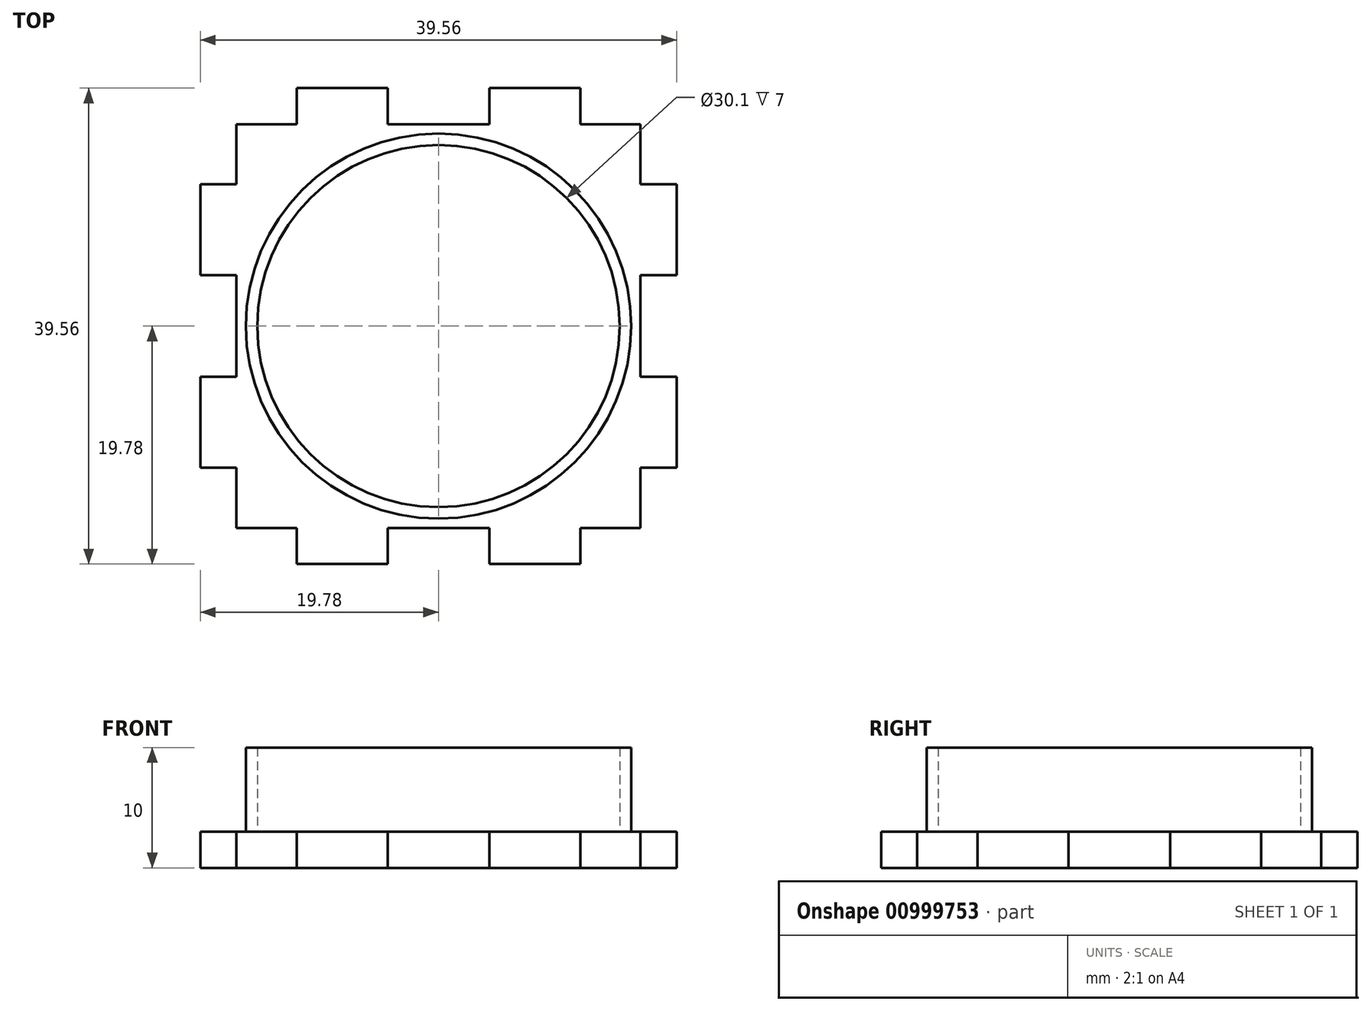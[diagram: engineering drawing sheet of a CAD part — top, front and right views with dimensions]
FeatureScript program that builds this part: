
annotation { "Feature Type Name" : "Feature", "Feature Type Description" : "" }
export const myFeature = defineFeature(function(context is Context, id is Id, definition is map)
    precondition{}
    {
        {
            var Q0;
            Q0=qCreatedBy(makeId("Top.planeOp"),FACE);
            var sketch = newSketch(context, id + "F0", { "sketchPlane" : qUnion([Q0])});
            skLineSegment(sketch, "E0.bottom", {"start": v(17, -17) * mm, "end": v(-17, -17) * mm});
            skLineSegment(sketch, "E0.top", {"start": v(17, 17) * mm, "end": v(-17, 17) * mm});
            skLineSegment(sketch, "E0.left", {"start": v(17, -17) * mm, "end": v(17, 17) * mm});
            skLineSegment(sketch, "E0.right", {"start": v(-17, -17) * mm, "end": v(-17, 17) * mm});
            skPoint(sketch, "E0.middle", {"position": v(0, 0) * mm});
            skSolve(sketch);
        }
        {
            var Q0;
            Q0=qSketchRegion(id+"F0",true);
            extrude(context, id + "F1", {"entities" : qUnion([Q0]), "depth" : 3 * mm, "offsetDistance" : 25 * mm});
        }
        {
            var Q0;
            Q0=makeQuery(id+"F1.opExtrude","CAP_FACE",FACE,{"disambiguationData":[OSD([sQuery(id+"F0.wireOp",EDGE,"E0.bottom"),sQuery(id+"F0.wireOp",EDGE,"E0.top"),sQuery(id+"F0.wireOp",EDGE,"E0.left"),sQuery(id+"F0.wireOp",EDGE,"E0.right")])],"isStart":false});
            var sketch = newSketch(context, id + "F2", { "sketchPlane" : qUnion([Q0])});
            skLineSegment(sketch, "E1.bottom", {"start": v(-17, 12) * mm, "end": v(-20, 12) * mm});
            skLineSegment(sketch, "E1.top", {"start": v(-17, 4) * mm, "end": v(-20, 4) * mm});
            skLineSegment(sketch, "E1.left", {"start": v(-17, 12) * mm, "end": v(-17, 4) * mm});
            skLineSegment(sketch, "E1.right", {"start": v(-20, 12) * mm, "end": v(-20, 4) * mm});
            skLineSegment(sketch, "E2.MirrorCS", {"start": v(-17, -12) * mm, "end": v(-20, -12) * mm});
            skLineSegment(sketch, "E3.MirrorCS", {"start": v(-17, -12) * mm, "end": v(-17, -4) * mm});
            skLineSegment(sketch, "E4.MirrorCS", {"start": v(-20, -12) * mm, "end": v(-20, -4) * mm});
            skLineSegment(sketch, "E5.MirrorCS", {"start": v(-17, -4) * mm, "end": v(-20, -4) * mm});
            skLineSegment(sketch, "E6.1.0", {"start": v(-4, -17) * mm, "end": v(-4, -20) * mm});
            skLineSegment(sketch, "E6.1.1", {"start": v(4, -17) * mm, "end": v(4, -20) * mm});
            skLineSegment(sketch, "E6.1.2", {"start": v(12, -17) * mm, "end": v(4, -17) * mm});
            skLineSegment(sketch, "E6.1.3", {"start": v(-12, -17) * mm, "end": v(-12, -20) * mm});
            skLineSegment(sketch, "E6.1.4", {"start": v(12, -17) * mm, "end": v(12, -20) * mm});
            skLineSegment(sketch, "E6.1.5", {"start": v(-12, -17) * mm, "end": v(-4, -17) * mm});
            skLineSegment(sketch, "E6.1.6", {"start": v(12, -20) * mm, "end": v(4, -20) * mm});
            skLineSegment(sketch, "E6.1.7", {"start": v(-12, -20) * mm, "end": v(-4, -20) * mm});
            skLineSegment(sketch, "E6.2.0", {"start": v(17, -4) * mm, "end": v(20, -4) * mm});
            skLineSegment(sketch, "E6.2.1", {"start": v(17, 4) * mm, "end": v(20, 4) * mm});
            skLineSegment(sketch, "E6.2.2", {"start": v(17, 12) * mm, "end": v(17, 4) * mm});
            skLineSegment(sketch, "E6.2.3", {"start": v(17, -12) * mm, "end": v(20, -12) * mm});
            skLineSegment(sketch, "E6.2.4", {"start": v(17, 12) * mm, "end": v(20, 12) * mm});
            skLineSegment(sketch, "E6.2.5", {"start": v(17, -12) * mm, "end": v(17, -4) * mm});
            skLineSegment(sketch, "E6.2.6", {"start": v(20, 12) * mm, "end": v(20, 4) * mm});
            skLineSegment(sketch, "E6.2.7", {"start": v(20, -12) * mm, "end": v(20, -4) * mm});
            skLineSegment(sketch, "E6.3.0", {"start": v(4, 17) * mm, "end": v(4, 20) * mm});
            skLineSegment(sketch, "E6.3.1", {"start": v(-4, 17) * mm, "end": v(-4, 20) * mm});
            skLineSegment(sketch, "E6.3.2", {"start": v(-12, 17) * mm, "end": v(-4, 17) * mm});
            skLineSegment(sketch, "E6.3.3", {"start": v(12, 17) * mm, "end": v(12, 20) * mm});
            skLineSegment(sketch, "E6.3.4", {"start": v(-12, 17) * mm, "end": v(-12, 20) * mm});
            skLineSegment(sketch, "E6.3.5", {"start": v(12, 17) * mm, "end": v(4, 17) * mm});
            skLineSegment(sketch, "E6.3.6", {"start": v(-12, 20) * mm, "end": v(-4, 20) * mm});
            skLineSegment(sketch, "E6.3.7", {"start": v(12, 20) * mm, "end": v(4, 20) * mm});
            skPoint(sketch, "E6.center", {"position": v(0, 0) * mm});
            skSolve(sketch);
        }
        {
            var Q0;
            Q0=qSketchRegion(id+"F2",true);
            extrude(context, id + "F3", {"entities" : qUnion([Q0]), "operationType" : NewBodyOperationType.ADD, "oppositeDirection" : true, "depth" : 3 * mm, "offsetDistance" : 25 * mm});
        }
        {
            var Q0;
            Q0=makeQuery(id+"F3.boolean.opBoolean","MERGE",FACE,{"derivedFrom":[makeQuery(id+"F1.opExtrude","CAP_FACE",FACE,{"disambiguationData":[OSD([sQuery(id+"F0.wireOp",EDGE,"E0.bottom"),sQuery(id+"F0.wireOp",EDGE,"E0.top"),sQuery(id+"F0.wireOp",EDGE,"E0.left"),sQuery(id+"F0.wireOp",EDGE,"E0.right")])],"isStart":false}),makeQuery(id+"F3.opExtrude","CAP_FACE",FACE,{"disambiguationData":[OSD([sQuery(id+"F2.wireOp",EDGE,"E1.bottom"),sQuery(id+"F2.wireOp",EDGE,"E1.top"),sQuery(id+"F2.wireOp",EDGE,"E1.left"),sQuery(id+"F2.wireOp",EDGE,"E1.right")])],"isStart":true}),makeQuery(id+"F3.opExtrude","CAP_FACE",FACE,{"disambiguationData":[OSD([sQuery(id+"F2.wireOp",EDGE,"E2.MirrorCS"),sQuery(id+"F2.wireOp",EDGE,"E3.MirrorCS"),sQuery(id+"F2.wireOp",EDGE,"E4.MirrorCS"),sQuery(id+"F2.wireOp",EDGE,"E5.MirrorCS")])],"isStart":true}),makeQuery(id+"F3.opExtrude","CAP_FACE",FACE,{"disambiguationData":[OSD([sQuery(id+"F2.wireOp",EDGE,"E6.1.0"),sQuery(id+"F2.wireOp",EDGE,"E6.1.3"),sQuery(id+"F2.wireOp",EDGE,"E6.1.5"),sQuery(id+"F2.wireOp",EDGE,"E6.1.7")])],"isStart":true}),makeQuery(id+"F3.opExtrude","CAP_FACE",FACE,{"disambiguationData":[OSD([sQuery(id+"F2.wireOp",EDGE,"E6.1.1"),sQuery(id+"F2.wireOp",EDGE,"E6.1.2"),sQuery(id+"F2.wireOp",EDGE,"E6.1.4"),sQuery(id+"F2.wireOp",EDGE,"E6.1.6")])],"isStart":true}),makeQuery(id+"F3.opExtrude","CAP_FACE",FACE,{"disambiguationData":[OSD([sQuery(id+"F2.wireOp",EDGE,"E6.2.0"),sQuery(id+"F2.wireOp",EDGE,"E6.2.3"),sQuery(id+"F2.wireOp",EDGE,"E6.2.5"),sQuery(id+"F2.wireOp",EDGE,"E6.2.7")])],"isStart":true}),makeQuery(id+"F3.opExtrude","CAP_FACE",FACE,{"disambiguationData":[OSD([sQuery(id+"F2.wireOp",EDGE,"E6.2.1"),sQuery(id+"F2.wireOp",EDGE,"E6.2.2"),sQuery(id+"F2.wireOp",EDGE,"E6.2.4"),sQuery(id+"F2.wireOp",EDGE,"E6.2.6")])],"isStart":true}),makeQuery(id+"F3.opExtrude","CAP_FACE",FACE,{"disambiguationData":[OSD([sQuery(id+"F2.wireOp",EDGE,"E6.3.0"),sQuery(id+"F2.wireOp",EDGE,"E6.3.3"),sQuery(id+"F2.wireOp",EDGE,"E6.3.5"),sQuery(id+"F2.wireOp",EDGE,"E6.3.7")])],"isStart":true}),makeQuery(id+"F3.opExtrude","CAP_FACE",FACE,{"disambiguationData":[OSD([sQuery(id+"F2.wireOp",EDGE,"E6.3.1"),sQuery(id+"F2.wireOp",EDGE,"E6.3.2"),sQuery(id+"F2.wireOp",EDGE,"E6.3.4"),sQuery(id+"F2.wireOp",EDGE,"E6.3.6")])],"isStart":true})]});
            var sketch = newSketch(context, id + "F4", { "sketchPlane" : qUnion([Q0])});
            skLineSegment(sketch, "E7.0", {"start": v(11.78, -16.78) * mm, "end": v(16.78, -16.78) * mm});
            skLineSegment(sketch, "E7.1", {"start": v(11.78, -19.78) * mm, "end": v(11.78, -16.78) * mm});
            skLineSegment(sketch, "E7.2", {"start": v(4.22, -19.78) * mm, "end": v(11.78, -19.78) * mm});
            skLineSegment(sketch, "E7.3", {"start": v(4.22, -16.78) * mm, "end": v(4.22, -19.78) * mm});
            skLineSegment(sketch, "E7.4", {"start": v(-4.22, -16.78) * mm, "end": v(4.22, -16.78) * mm});
            skLineSegment(sketch, "E7.5", {"start": v(-4.22, -19.78) * mm, "end": v(-4.22, -16.78) * mm});
            skLineSegment(sketch, "E7.6", {"start": v(-11.78, -19.78) * mm, "end": v(-4.22, -19.78) * mm});
            skLineSegment(sketch, "E7.7", {"start": v(-11.78, -16.78) * mm, "end": v(-11.78, -19.78) * mm});
            skLineSegment(sketch, "E7.8", {"start": v(-16.78, -16.78) * mm, "end": v(-11.78, -16.78) * mm});
            skLineSegment(sketch, "E7.9", {"start": v(-16.78, -11.78) * mm, "end": v(-16.78, -16.78) * mm});
            skLineSegment(sketch, "E7.10", {"start": v(-19.78, -11.78) * mm, "end": v(-16.78, -11.78) * mm});
            skLineSegment(sketch, "E7.11", {"start": v(16.78, -16.78) * mm, "end": v(16.78, -11.78) * mm});
            skLineSegment(sketch, "E7.12", {"start": v(-19.78, -4.22) * mm, "end": v(-19.78, -11.78) * mm});
            skLineSegment(sketch, "E7.13", {"start": v(-16.78, -4.22) * mm, "end": v(-19.78, -4.22) * mm});
            skLineSegment(sketch, "E7.14", {"start": v(11.78, 16.78) * mm, "end": v(11.78, 19.78) * mm});
            skLineSegment(sketch, "E7.15", {"start": v(16.78, 16.78) * mm, "end": v(11.78, 16.78) * mm});
            skLineSegment(sketch, "E7.16", {"start": v(16.78, 11.78) * mm, "end": v(16.78, 16.78) * mm});
            skLineSegment(sketch, "E7.17", {"start": v(19.78, 11.78) * mm, "end": v(16.78, 11.78) * mm});
            skLineSegment(sketch, "E7.18", {"start": v(19.78, 4.22) * mm, "end": v(19.78, 11.78) * mm});
            skLineSegment(sketch, "E7.19", {"start": v(16.78, 4.22) * mm, "end": v(19.78, 4.22) * mm});
            skLineSegment(sketch, "E7.20", {"start": v(16.78, -11.78) * mm, "end": v(19.78, -11.78) * mm});
            skLineSegment(sketch, "E7.21", {"start": v(19.78, -11.78) * mm, "end": v(19.78, -4.22) * mm});
            skLineSegment(sketch, "E7.22", {"start": v(19.78, -4.22) * mm, "end": v(16.78, -4.22) * mm});
            skLineSegment(sketch, "E7.23", {"start": v(16.78, -4.22) * mm, "end": v(16.78, 4.22) * mm});
            skLineSegment(sketch, "E7.24", {"start": v(11.78, 19.78) * mm, "end": v(4.22, 19.78) * mm});
            skLineSegment(sketch, "E7.25", {"start": v(4.22, 19.78) * mm, "end": v(4.22, 16.78) * mm});
            skLineSegment(sketch, "E7.26", {"start": v(4.22, 16.78) * mm, "end": v(-4.22, 16.78) * mm});
            skLineSegment(sketch, "E7.27", {"start": v(-4.22, 16.78) * mm, "end": v(-4.22, 19.78) * mm});
            skLineSegment(sketch, "E7.28", {"start": v(-4.22, 19.78) * mm, "end": v(-11.78, 19.78) * mm});
            skLineSegment(sketch, "E7.29", {"start": v(-11.78, 19.78) * mm, "end": v(-11.78, 16.78) * mm});
            skLineSegment(sketch, "E7.30", {"start": v(-11.78, 16.78) * mm, "end": v(-16.78, 16.78) * mm});
            skLineSegment(sketch, "E7.31", {"start": v(-16.78, 16.78) * mm, "end": v(-16.78, 11.78) * mm});
            skLineSegment(sketch, "E7.32", {"start": v(-16.78, 11.78) * mm, "end": v(-19.78, 11.78) * mm});
            skLineSegment(sketch, "E7.33", {"start": v(-19.78, 11.78) * mm, "end": v(-19.78, 4.22) * mm});
            skLineSegment(sketch, "E7.34", {"start": v(-19.78, 4.22) * mm, "end": v(-16.78, 4.22) * mm});
            skLineSegment(sketch, "E7.35", {"start": v(-16.78, 4.22) * mm, "end": v(-16.78, -4.22) * mm});
            skLineSegment(sketch, "E8.bottom", {"start": v(25.94, -26.08) * mm, "end": v(-25.94, -26.08) * mm});
            skLineSegment(sketch, "E8.top", {"start": v(25.94, 26.08) * mm, "end": v(-25.94, 26.08) * mm});
            skLineSegment(sketch, "E8.left", {"start": v(25.94, -26.08) * mm, "end": v(25.94, 26.08) * mm});
            skLineSegment(sketch, "E8.right", {"start": v(-25.94, -26.08) * mm, "end": v(-25.94, 26.08) * mm});
            skPoint(sketch, "E8.middle", {"position": v(0, 0) * mm});
            skSolve(sketch);
        }
        {
            var Q0;
            Q0=qSketchRegion(id+"F4",true);
            extrude(context, id + "F5", {"entities" : qUnion([Q0]), "operationType" : NewBodyOperationType.REMOVE, "endBound" : BoundingType.THROUGH_ALL, "oppositeDirection" : true, "depth" : 25 * mm, "offsetDistance" : 25 * mm});
        }
        {
            var Q0;
            Q0=makeQuery(id+"F3.boolean.opBoolean","MERGE",FACE,{"derivedFrom":[makeQuery(id+"F1.opExtrude","CAP_FACE",FACE,{"disambiguationData":[OSD([sQuery(id+"F0.wireOp",EDGE,"E0.bottom"),sQuery(id+"F0.wireOp",EDGE,"E0.top"),sQuery(id+"F0.wireOp",EDGE,"E0.left"),sQuery(id+"F0.wireOp",EDGE,"E0.right")])],"isStart":false}),makeQuery(id+"F3.opExtrude","CAP_FACE",FACE,{"disambiguationData":[OSD([sQuery(id+"F2.wireOp",EDGE,"E1.bottom"),sQuery(id+"F2.wireOp",EDGE,"E1.top"),sQuery(id+"F2.wireOp",EDGE,"E1.left"),sQuery(id+"F2.wireOp",EDGE,"E1.right")])],"isStart":true}),makeQuery(id+"F3.opExtrude","CAP_FACE",FACE,{"disambiguationData":[OSD([sQuery(id+"F2.wireOp",EDGE,"E2.MirrorCS"),sQuery(id+"F2.wireOp",EDGE,"E3.MirrorCS"),sQuery(id+"F2.wireOp",EDGE,"E4.MirrorCS"),sQuery(id+"F2.wireOp",EDGE,"E5.MirrorCS")])],"isStart":true}),makeQuery(id+"F3.opExtrude","CAP_FACE",FACE,{"disambiguationData":[OSD([sQuery(id+"F2.wireOp",EDGE,"E6.1.0"),sQuery(id+"F2.wireOp",EDGE,"E6.1.3"),sQuery(id+"F2.wireOp",EDGE,"E6.1.5"),sQuery(id+"F2.wireOp",EDGE,"E6.1.7")])],"isStart":true}),makeQuery(id+"F3.opExtrude","CAP_FACE",FACE,{"disambiguationData":[OSD([sQuery(id+"F2.wireOp",EDGE,"E6.1.1"),sQuery(id+"F2.wireOp",EDGE,"E6.1.2"),sQuery(id+"F2.wireOp",EDGE,"E6.1.4"),sQuery(id+"F2.wireOp",EDGE,"E6.1.6")])],"isStart":true}),makeQuery(id+"F3.opExtrude","CAP_FACE",FACE,{"disambiguationData":[OSD([sQuery(id+"F2.wireOp",EDGE,"E6.2.0"),sQuery(id+"F2.wireOp",EDGE,"E6.2.3"),sQuery(id+"F2.wireOp",EDGE,"E6.2.5"),sQuery(id+"F2.wireOp",EDGE,"E6.2.7")])],"isStart":true}),makeQuery(id+"F3.opExtrude","CAP_FACE",FACE,{"disambiguationData":[OSD([sQuery(id+"F2.wireOp",EDGE,"E6.2.1"),sQuery(id+"F2.wireOp",EDGE,"E6.2.2"),sQuery(id+"F2.wireOp",EDGE,"E6.2.4"),sQuery(id+"F2.wireOp",EDGE,"E6.2.6")])],"isStart":true}),makeQuery(id+"F3.opExtrude","CAP_FACE",FACE,{"disambiguationData":[OSD([sQuery(id+"F2.wireOp",EDGE,"E6.3.0"),sQuery(id+"F2.wireOp",EDGE,"E6.3.3"),sQuery(id+"F2.wireOp",EDGE,"E6.3.5"),sQuery(id+"F2.wireOp",EDGE,"E6.3.7")])],"isStart":true}),makeQuery(id+"F3.opExtrude","CAP_FACE",FACE,{"disambiguationData":[OSD([sQuery(id+"F2.wireOp",EDGE,"E6.3.1"),sQuery(id+"F2.wireOp",EDGE,"E6.3.2"),sQuery(id+"F2.wireOp",EDGE,"E6.3.4"),sQuery(id+"F2.wireOp",EDGE,"E6.3.6")])],"isStart":true})]});
            var sketch = newSketch(context, id + "F6", { "sketchPlane" : qUnion([Q0])});
            skCircle(sketch, "E9", {"center": v(0, 0) * mm, "radius": 15.05 * mm});
            skCircle(sketch, "E10", {"center": v(0, 0) * mm, "radius": 16 * mm});
            skSolve(sketch);
        }
        {
            var Q0;
            Q0 = qSketchRegion(id + "F6", true);
            extrude(context, id + "F7", {"entities" : qUnion([Q0]), "operationType" : NewBodyOperationType.ADD, "depth" : 7 * mm, "offsetDistance" : 25 * mm});
        }
    });
